FCSTD DOCUMENT  (FreeCAD 2024.408R14555 (Git shallow))
Label: vacuum table - large sieve
License: All rights reserved
LicenseURL: https://en.wikipedia.org/wiki/All_rights_reserved
objects: Sketcher::SketchObject×2, Part::Part2DObjectPython×2, PartDesign::Pad×2, PartDesign::FeaturePython×2, Spreadsheet::Sheet×1, App::Link×1, PartDesign::SubShapeBinder×1, PartDesign::Body×1, Mesh::Feature×1
note: 18 computed .brp shape members not serialized (recipe doc carries the construction recipe); baked Part::Feature solids carry a one-line shape summary decoded from their .brp
EXTERNAL_REF file=vacuum table.FCStd obj=Pad008
EXTERNAL_REF file=vacuum table.FCStd obj=Spreadsheet

FEATURE [Spreadsheet::Sheet] Spreadsheet  label="dim"
  PythonMode = false
  ShowCells = 0
  TreeRank = 1
  cells = A1=layer_height; B1(layer_height)==0.2 mm; A2=extrusion_width; B2(extrusion_width)==0.5 mm; A4=inner_d_low; B4(inner_d_low)==33.5 mm; A5=inner_d_high; B5(inner_d_high)==36.5 mm; D5=outer_d_high; E5(outer_d_high)==inner_d_high + 2 * wall; A6=adapter_length; B6(adapter_length)==70 mm; A7=wall; B7(wall)==1.8 mm; A9=tool_mount_d_delta; B9(tool_mount_d_delta)==6 mm; D9=tool_mount_d; E9(tool_mount_d)==inner_d_low + tool_mount_d_delta; A10=tool_mount_length; B10(tool_mount_length)==10 mm; A11=tool_mount_slack; B11(tool_mount_slack)==0.5 mm; D11=tool_d; E11(tool_d)==tool_mount_d - tool_mount_slack; A12=tool_mount_fillet_angle; B12(tool_mount_fillet_angle)==40 deg; A13=tool_base_chamfer; B13(tool_base_chamfer)==1 mm; A14=tool_top_grab_thickness; B14(tool_top_grab_thickness)==5 mm; A15=tool_inset; B15(tool_inset)==2 mm; A17=large_tool_side; B17(large_tool_side)==100 mm; A18=large_tool_fillet; B18(large_tool_fillet)==8 mm; A19=large_tool_length; B19(large_tool_length)==50 mm; A20=large_tool_top_wall; B20(large_tool_top_wall)==3 mm; A21=large_tool_side_clamp_size; B21(large_tool_side_clamp_size)==20 mm; A23=sieve_hole; B23(sieve_hole)==1.5 mm; D23=num_holes; E23(num_holes)==round(inner_d_low / (sieve_hole + sieve_mesh)); A24=sieve_mesh; B24(sieve_mesh)==0.9 mm; D24=hole_offset; E24(hole_offset)==num_holes / 2 * (sieve_hole + sieve_mesh); A25=sieve_thickness; B25(sieve_thickness)==2 mm; A27=flange_d_delta; B27(flange_d_delta)==3 mm; D27=outer_d_flange; E27(outer_d_flange)==outer_d_high + flange_d_delta * 2; A28=flange_length; B28(flange_length)==20 mm; A30=mount_d_slack; B30(mount_d_slack)==0.5 mm; D30=mount_inner_d; E30(mount_inner_d)==<<dim>>.outer_d_high + mount_d_slack; A31=mount_wall; B31(mount_wall)==4 mm; D31=mount_outer_d; E31(mount_outer_d)==mount_inner_d + 2 * mount_wall; A32=mount_length; B32(mount_length)==30 mm; A33=mount_width; B33(mount_width)==120 mm; A34=mount_depth; B34(mount_depth)==60 mm; A35=mount_fillet; B35(mount_fillet)==5 mm; A36=mount_thickness; B36(mount_thickness)==5 mm; A38=mount_fins_width; B38(mount_fins_width)==8 mm; A39=mount_fins_distance; B39(mount_fins_distance)==18 mm; A41=mount_internal_hole_z_offset; B41(mount_internal_hole_z_offset)==1 mm; D41=mount_internal_hole_height; E41(mount_internal_hole_height)==mount_thickness - 2 * mount_internal_hole_z_offset; A42=mount_internal_hole_side_offset; B42(mount_internal_hole_side_offset)==6 mm; A43=mount_internal_hole_count; B43(mount_internal_hole_count)=5; A44=mount_internal_hole_distance; B44(mount_internal_hole_distance)==10 mm
FEATURE [Sketcher::SketchObject] Sketch020
  ArcFitTolerance = 1e-06
  AttachmentOffset = pos=(-47,52,-3) rot=(0,0,1;0rad)
  AttachmentSupport = -> [XZ_Plane006]
  ExternalBSplineMaxDegree = 5
  ExternalBSplineTolerance = 0.0001
  FixShape = 1
  FullyConstrained = true
  InternalTolerance = 1e-06
  InvalidShape = false
  MakeInternals = false
  MapMode = 5
  Placement = pos=(-47,3,52) rot=(1,0,0;1.5708rad)
  Support = -> [XZ_Plane006]
  TreeRank = 205
  ValidateShape = false
  expr: AttachmentOffset.Base.x = -<<dim>>.large_tool_side / 2 + <<dim>>.large_tool_top_wall
  expr: AttachmentOffset.Base.y = <<dim>>.large_tool_length + <<dim>>.sieve_thickness
  expr: AttachmentOffset.Base.z = -<<dim>>.large_tool_top_wall
  expr: Constraints[20] = <<dim>>.extrusion_width
  expr: Constraints[21] = <<dim>>.sieve_mesh
  expr: Constraints[22] = <<dim>>.sieve_thickness
  sketch-geometry (8):
    g0: LineSegment StartX=-0.25 StartY=0 StartZ=0 EndX=0.25 EndY=0 EndZ=0
    g1: LineSegment StartX=0.25 StartY=0 StartZ=0 EndX=0.45 EndY=-0.2 EndZ=0
    g2: LineSegment StartX=0.45 StartY=-0.2 StartZ=0 EndX=0.45 EndY=-1.8 EndZ=0
    g3: LineSegment StartX=0.45 StartY=-1.8 StartZ=0 EndX=0.25 EndY=-2 EndZ=0
    g4: LineSegment StartX=0.25 StartY=-2 StartZ=0 EndX=-0.25 EndY=-2 EndZ=0
    g5: LineSegment StartX=-0.25 StartY=-2 StartZ=0 EndX=-0.45 EndY=-1.8 EndZ=0
    g6: LineSegment StartX=-0.45 StartY=-1.8 StartZ=0 EndX=-0.45 EndY=-0.2 EndZ=0
    g7: LineSegment StartX=-0.45 StartY=-0.2 StartZ=0 EndX=-0.25 EndY=0 EndZ=0
  constraints (23):
    c: PointOnObject(g0,g-1)
    c: PointOnObject(g0,g-1)
    c: Coincident(g0,g1)
    c: Coincident(g1,g2)
    c: Vertical(g2)
    c: Coincident(g2,g3)
    c: Coincident(g3,g4)
    c: Coincident(g4,g5)
    c: Coincident(g5,g6)
    c: Vertical(g6)
    c: Coincident(g6,g7)
    c: Coincident(g7,g0)
    c: Horizontal(g4)
    c: Parallel(g3,g7)
    c: Parallel(g5,g1)
    c: Perpendicular(g1,g7)
    c: Angle(g3) = -2.35619
    c: Symmetric(g6,g1,g-2)
    c: Equal(g0,g4)
    c: Vertical(g4,g0)
    c: DistanceX(g0,g0) = 0.5
    c: DistanceX(g6,g1) = 0.9
    c: DistanceY(g3,g0) = 2
FEATURE [Part::Part2DObjectPython] LinearArray002  # Draft 2D object (typed FeaturePython)
  Alignment = 0
  AttacherType = Attacher::AttachEngine3D
  CellStart = A1
  Count = 40
  Dir = (1,0,0)
  DirIsDriven = true
  DistributionLaw = 0
  DrivenProperty = 1
  EndInclusive = true
  ExposePlacement = false
  FixShape = 1
  GeneratorMode = 2
  InvalidShape = false
  MarkerShape = 1
  MarkerSize = 0
  NumElements = 40
  OrientMode = 1
  Point = (0,0,0)
  PointIsDriven = true
  Reverse = false
  SpanEnd = 94
  SpanStart = 0
  Step = 2.4
  TreeRank = 202
  Type = lattice2LinearArray.LinearArray
  VSGVersion = 1
  ValidateShape = false
  Values = 0.0 | 2.4 | 4.8 | 7.199999999999999 | 9.6 | 12.0 | 14.399999999999999 | 16.8 | 19.2 | 21.599999999999998 | 24.0 | 26.4 | 28.799999999999997 | 31.2 | 33.6 | 36.0 | 38.4 | 40.8 | 43.199999999999996 | 45.6 | 48.0 | 50.4 | 52.8 | 55.199999999999996 | 57.599999999999994 | 60.0 | 62.4 | 64.8 | 67.2 | 69.6 | 72.0 | 74.39999999999999 | 76.8 | 79.2 | 81.6 | 84.0 | 86.39999999999999 | 88.8 | 91.2 | 93.6
  ValuesSource = 2
  isLattice = 1
  expr: SpanEnd = <<dim>>.large_tool_side - 2 * <<dim>>.large_tool_top_wall
  expr: Step = <<dim>>.sieve_hole + <<dim>>.sieve_mesh
FEATURE [Sketcher::SketchObject] Sketch021
  ArcFitTolerance = 1e-06
  AttachmentOffset = pos=(-47,52,-3) rot=(0,0,1;0rad)
  AttachmentSupport = -> [YZ_Plane006]
  ExternalBSplineMaxDegree = 5
  ExternalBSplineTolerance = 0.0001
  FixShape = 1
  FullyConstrained = true
  InternalTolerance = 1e-06
  InvalidShape = false
  MakeInternals = false
  MapMode = 5
  Placement = pos=(-3,-47,52) rot=(0.57735,0.57735,0.57735;2.0944rad)
  Support = -> [YZ_Plane006]
  TreeRank = 192
  ValidateShape = false
  expr: AttachmentOffset.Base.x = -<<dim>>.large_tool_side / 2 + <<dim>>.large_tool_top_wall
  expr: AttachmentOffset.Base.y = <<dim>>.large_tool_length + <<dim>>.sieve_thickness
  expr: AttachmentOffset.Base.z = -<<dim>>.large_tool_top_wall
  expr: Constraints[20] = <<dim>>.extrusion_width
  expr: Constraints[21] = <<dim>>.sieve_mesh
  expr: Constraints[22] = <<dim>>.sieve_thickness
  sketch-geometry (8):
    g0: LineSegment StartX=-0.25 StartY=0 StartZ=0 EndX=0.25 EndY=0 EndZ=0
    g1: LineSegment StartX=0.25 StartY=0 StartZ=0 EndX=0.45 EndY=-0.2 EndZ=0
    g2: LineSegment StartX=0.45 StartY=-0.2 StartZ=0 EndX=0.45 EndY=-1.8 EndZ=0
    g3: LineSegment StartX=0.45 StartY=-1.8 StartZ=0 EndX=0.25 EndY=-2 EndZ=0
    g4: LineSegment StartX=0.25 StartY=-2 StartZ=0 EndX=-0.25 EndY=-2 EndZ=0
    g5: LineSegment StartX=-0.25 StartY=-2 StartZ=0 EndX=-0.45 EndY=-1.8 EndZ=0
    g6: LineSegment StartX=-0.45 StartY=-1.8 StartZ=0 EndX=-0.45 EndY=-0.2 EndZ=0
    g7: LineSegment StartX=-0.45 StartY=-0.2 StartZ=0 EndX=-0.25 EndY=0 EndZ=0
  constraints (23):
    c: PointOnObject(g0,g-1)
    c: PointOnObject(g0,g-1)
    c: Coincident(g0,g1)
    c: Coincident(g1,g2)
    c: Vertical(g2)
    c: Coincident(g2,g3)
    c: Coincident(g3,g4)
    c: Coincident(g4,g5)
    c: Coincident(g5,g6)
    c: Vertical(g6)
    c: Coincident(g6,g7)
    c: Coincident(g7,g0)
    c: Horizontal(g4)
    c: Parallel(g3,g7)
    c: Parallel(g5,g1)
    c: Perpendicular(g1,g7)
    c: Angle(g3) = -2.35619
    c: Symmetric(g6,g1,g-2)
    c: Equal(g0,g4)
    c: Vertical(g4,g0)
    c: DistanceX(g0,g0) = 0.5
    c: DistanceX(g6,g1) = 0.9
    c: DistanceY(g3,g0) = 2
FEATURE [Part::Part2DObjectPython] LinearArray003  # Draft 2D object (typed FeaturePython)
  Alignment = 0
  AttacherType = Attacher::AttachEngine3D
  CellStart = A1
  Count = 40
  Dir = (0,1,0)
  DirIsDriven = true
  DistributionLaw = 0
  DrivenProperty = 1
  EndInclusive = true
  ExposePlacement = false
  FixShape = 1
  GeneratorMode = 2
  InvalidShape = false
  MarkerShape = 1
  MarkerSize = 0
  NumElements = 40
  OrientMode = 1
  Point = (0,0,0)
  PointIsDriven = true
  Reverse = false
  SpanEnd = 94
  SpanStart = 0
  Step = 2.4
  TreeRank = 201
  Type = lattice2LinearArray.LinearArray
  VSGVersion = 1
  ValidateShape = false
  Values = 0.0 | 2.4 | 4.8 | 7.199999999999999 | 9.6 | 12.0 | 14.399999999999999 | 16.8 | 19.2 | 21.599999999999998 | 24.0 | 26.4 | 28.799999999999997 | 31.2 | 33.6 | 36.0 | 38.4 | 40.8 | 43.199999999999996 | 45.6 | 48.0 | 50.4 | 52.8 | 55.199999999999996 | 57.599999999999994 | 60.0 | 62.4 | 64.8 | 67.2 | 69.6 | 72.0 | 74.39999999999999 | 76.8 | 79.2 | 81.6 | 84.0 | 86.39999999999999 | 88.8 | 91.2 | 93.6
  ValuesSource = 2
  isLattice = 1
  expr: SpanEnd = <<dim>>.large_tool_side - 2 * <<dim>>.large_tool_top_wall
  expr: Step = <<dim>>.sieve_hole + <<dim>>.sieve_mesh
FEATURE [App::Link] Link  label="Link(Pad008)"
  AutoLinkLabel = true
  AutoPlacement = true
  LinkPlacement = pos=(0,0,-5) rot=(0,0,1;0rad)
  LinkedObject = -> <external vacuum table.FCStd>#Pad008
  Placement = pos=(0,0,-5) rot=(0,0,1;0rad)
  SyncGroupVisibility = false
  TreeRank = 203
  _LinkVersion = 1
FEATURE [PartDesign::SubShapeBinder] Binder  label="Binder(*Pad008)"
  BindCopyOnChange = 0
  BindMode = 0
  ClaimChildren = false
  Context = -> Body006 [Binder.]
  EdgeTolerance = 1e-06
  FillStyle = 0
  FixShape = 1
  Fuse = false
  InvalidShape = false
  MakeFace = true
  MergeEdges = true
  OffsetFill = false
  OffsetIntersection = false
  OffsetJoinType = 0
  OffsetOpenResult = false
  Outline = false
  PartialLoad = false
  Relative = true
  SplitEdges = false
  Support = -> [Link[Face38]]
  TightBound = false
  TreeRank = 204
  ValidateShape = false
  _Version = 8
FEATURE [PartDesign::Pad] Pad
  AddSubType = 0
  AlongSketchNormal = false
  AutoTaperInnerAngle = true
  CheckUpToFaceLimits = true
  ClaimChildren = false
  Direction = (0,-1,-2e-16)
  Fit = 0
  FitJoin = 0
  FixShape = 1
  InnerFit = 0
  InnerFitJoin = 0
  InvalidShape = false
  Length = 100
  Length2 = 10
  Linearize = true
  Midplane = true
  NewSolid = false
  Profile = -> Sketch020
  ReferenceAxis = -> Sketch020 [N_Axis]
  Refine = true
  Suppress = false
  TaperInnerAngle = 0
  TaperInnerAngleRev = 0
  TreeRank = 206
  Type = 0
  ValidateShape = false
  _ProfileBasedVersion = 1
  expr: Length = <<vacuum table>>#<<dim>>.large_tool_side
FEATURE [PartDesign::Pad] Pad001
  AddSubType = 0
  AlongSketchNormal = false
  AutoTaperInnerAngle = true
  BaseFeature = -> Pad
  CheckUpToFaceLimits = true
  ClaimChildren = false
  Direction = (1,-2e-16,3e-16)
  Fit = 0
  FitJoin = 0
  FixShape = 1
  InnerFit = 0
  InnerFitJoin = 0
  InvalidShape = false
  Length = 100
  Length2 = 10
  Linearize = true
  Midplane = true
  NewSolid = false
  Profile = -> Sketch021
  ReferenceAxis = -> Sketch021 [N_Axis]
  Refine = true
  Suppress = false
  TaperInnerAngle = 0
  TaperInnerAngleRev = 0
  TreeRank = 207
  Type = 0
  ValidateShape = false
  _ProfileBasedVersion = 1
  expr: Length = <<Pad>>.Length
FEATURE [PartDesign::FeaturePython] LatticePattern  # WARN: FeaturePython — macro-defined, semantics opaque (R4)
  BaseFeature = -> Pad001
  FeaturesToCopy = -> [Pad]
  FixShape = 1
  IgnoreUnsupported = false
  InvalidShape = false
  NewSolid = false
  PlacementsTo = -> LinearArray002
  Referencing = 1
  Selfintersections = false
  SignOverride = 0
  SkipFirstInBody = false
  Suppress = false
  TreeRank = 208
  ValidateShape = false
FEATURE [PartDesign::FeaturePython] LatticePattern001  # WARN: FeaturePython — macro-defined, semantics opaque (R4)
  BaseFeature = -> LatticePattern
  FeaturesToCopy = -> [Pad001]
  FixShape = 1
  IgnoreUnsupported = false
  InvalidShape = false
  NewSolid = false
  PlacementsTo = -> LinearArray003
  Referencing = 1
  Selfintersections = false
  SignOverride = 0
  SkipFirstInBody = false
  Suppress = false
  TreeRank = 209
  ValidateShape = false
FEATURE [PartDesign::Body] Body006  label="large_sieve"
  AutoGroupSolids = false
  ClaimAllChildren = false
  ExportMode = 0
  FixShape = 1
  Group = -> [Sketch020,LinearArray002,Sketch021,LinearArray003,Binder,Pad,Pad001,LatticePattern,LatticePattern001]
  InvalidShape = false
  Origin = -> Origin006
  Tip = -> LatticePattern001
  TreeRank = 186
  ValidateShape = false
  _ExportChildren = -> [Binder,Pad,Pad001,LatticePattern,LatticePattern001]
  _GroupVersion = 1
FEATURE [Mesh::Feature] Mesh  label="large_sieve (Meshed)"
  TreeRank = 210
